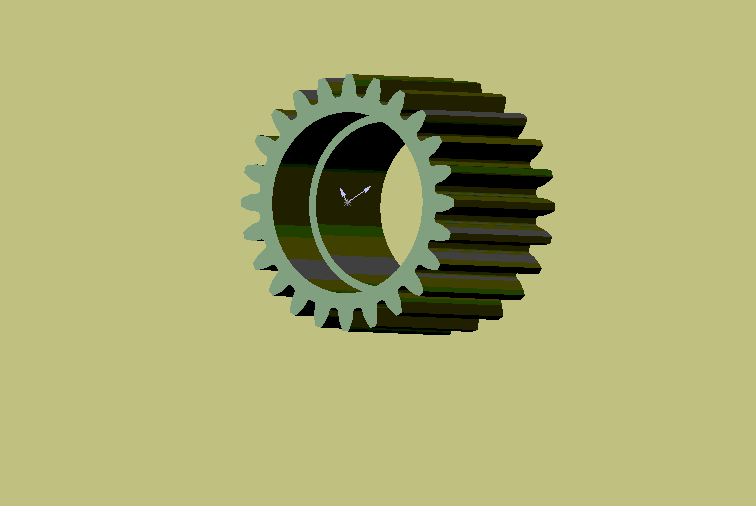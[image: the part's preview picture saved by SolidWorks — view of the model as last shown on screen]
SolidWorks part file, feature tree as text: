
SOLIDWORKS PART (.sldprt)
format: sldprt  version: not decoded by parser v0  size: 363,008 bytes
history: native  units: mm
features: sketch x20, plane x4, cut_extrude x2, material x1, fillet x1, pattern_circular x1 (+8 scaffold rows collapsed)
feature tree (37):
  scaffold x8  (default folders/planes/origin — collapsed)
  material  "Matériau <non spécifié>"
  plane  "Plane1"
  plane  "Plane2"
  plane  "Plane3"
  sketch  "Esquisse1"  dims[c1.D2=7.2mm c1.D1=42.0mm c2.D1=7.5deg]
  sketch  "Esquisse2"  dims[c1.D2=~7.055262mm c1.D1=37.0mm c2.D1=~8.269674deg]
  sketch  "Esquisse3"  dims[c1.D2=~6.910525mm c1.D1=33.0mm c2.D1=~8.873081deg]
  sketch  "Esquisse4"  dims[c1.D2=~6.765787mm c1.D1=30.0mm c2.D1=~9.207917deg]
  sketch  "Esquisse5"  dims[c1.D2=7.4mm c1.D1=46.0mm c2.D1=~6.230236deg]
  sketch  "Esquisse6"  dims[c1.D2=7.6mm c1.D1=50.0mm c2.D1=~4.769923deg]
  sketch  "Esquisse7"  dims[c1.D2=7.8mm c1.D1=54.0mm c2.D1=~3.153694deg]
  plane  "Plan1"  Offset=11mm
  sketch  "Esquisse8"  dims[c1.D2=7.2mm c1.D1=18.0mm c2.D1=7.5deg]
  sketch  "Esquisse9"  dims[c1.D2=~7.055262mm c1.D1=15.0mm c2.D1=~8.269674deg]
  sketch  "Esquisse10"  dims[c1.D2=~6.910525mm c1.D1=13.0mm c2.D1=~8.873081deg]
  sketch  "Esquisse11"  dims[c1.D2=~6.765787mm c1.D1=12.0mm c2.D1=~9.207917deg]
  sketch  "Esquisse12"  dims[c1.D2=7.4mm c1.D1=20.0mm c2.D1=~6.230236deg]
  sketch  "Esquisse13"  dims[c1.D2=7.6mm c1.D1=21.0mm c2.D1=~4.769923deg]
  sketch  "Esquisse14"  dims[c1.D2=7.8mm c1.D1=22.0mm c2.D1=~3.153694deg]
  sketch  "Esquisse15"  dims[c1.D2=6.45mm c1.D1=23.0mm c2.D1=~9.207917deg]
  sketch  "Esquisse16"  dims[c1.D2=6.45mm c1.D1=10.0mm c2.D1=~9.207917deg]
  sketch  "Esquisse17"  dims[D1=12.9mm]
  sketch  "Esquisse18"  dims[D1=12.9mm]
  fillet  "Congé1"  Radius=0.25mm
  pattern_circular  "Répétition circulaire1"  Count=24 Angle=360deg
  sketch  "Esquisse19"  dims[D1=10.0mm]
  cut_extrude  "Enlèv. mat.-Extru.1"  [1 undecoded]
  sketch  "Esquisse20"  dims[D1=11.0mm]
  cut_extrude  "Enlèv. mat.-Extru.2"  Depth=4mm
decode coverage: 23 of 24 modeling features carry decoded parameters
note: ~ marks probable driven/reference dimensions
note: 1 parameter value undecoded
note: suppression state not decoded; provenance and decode notes live in map.json
